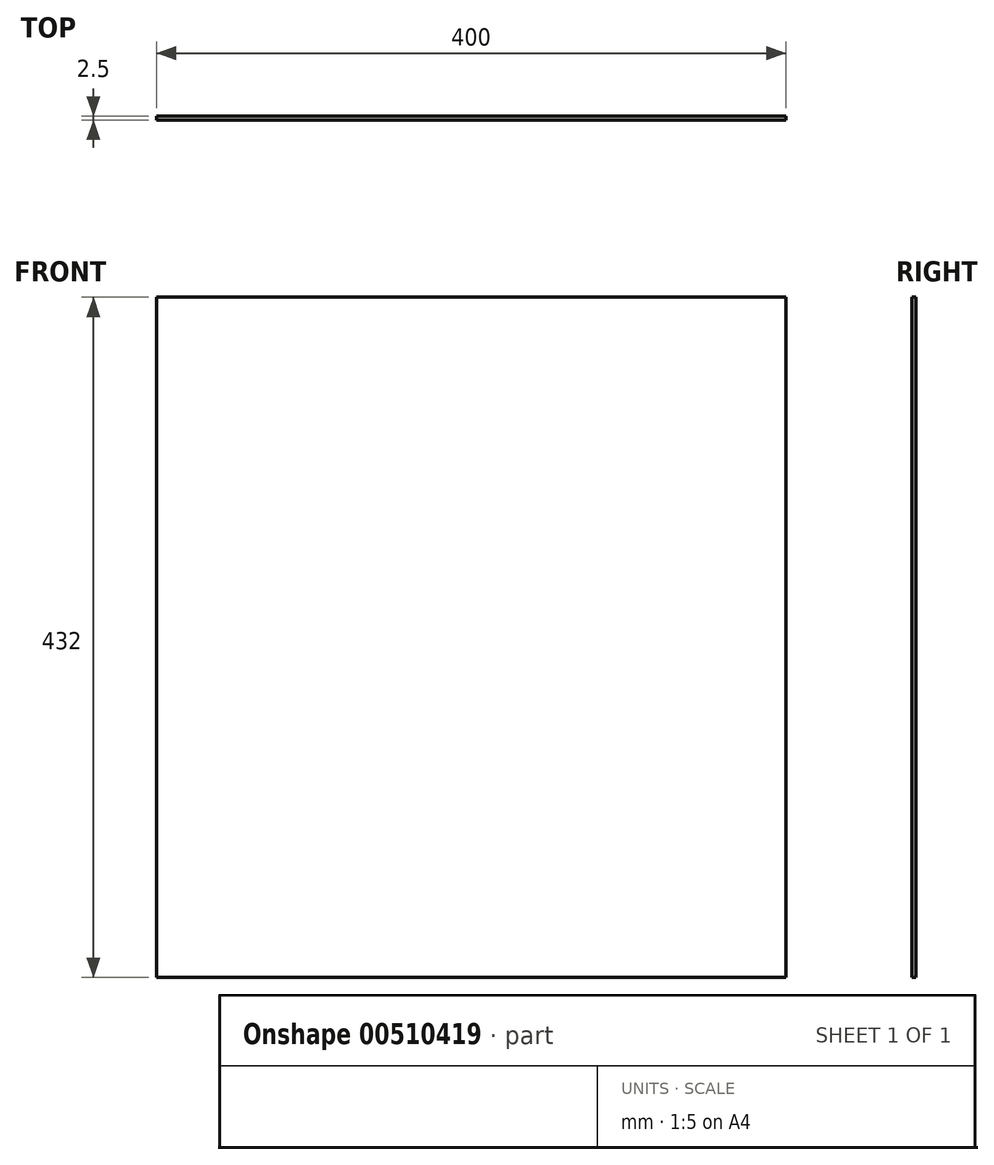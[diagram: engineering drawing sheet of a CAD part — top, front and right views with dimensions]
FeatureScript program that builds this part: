
annotation { "Feature Type Name" : "Feature", "Feature Type Description" : "" }
export const myFeature = defineFeature(function(context is Context, id is Id, definition is map)
    precondition{}
    {
        {
            var Q0;
            Q0=qCreatedBy(makeId("Front.planeOp"),FACE);
            var sketch = newSketch(context, id + "F0", { "sketchPlane" : qUnion([Q0])});
            skLineSegment(sketch, "E0.bottom", {"start": v(-343.97, 387.47) * mm, "end": v(56.03, 387.47) * mm});
            skLineSegment(sketch, "E0.top", {"start": v(-343.97, -44.53) * mm, "end": v(56.03, -44.53) * mm});
            skLineSegment(sketch, "E0.left", {"start": v(-343.97, 387.47) * mm, "end": v(-343.97, -44.53) * mm});
            skLineSegment(sketch, "E0.right", {"start": v(56.03, 387.47) * mm, "end": v(56.03, -44.53) * mm});
            skSolve(sketch);
        }
        {
            var Q0;
            Q0 = qSketchRegion(id + "F0", true);
            extrude(context, id + "F1", {"entities" : qUnion([Q0]), "depth" : 2.5 * mm});
        }
    });
